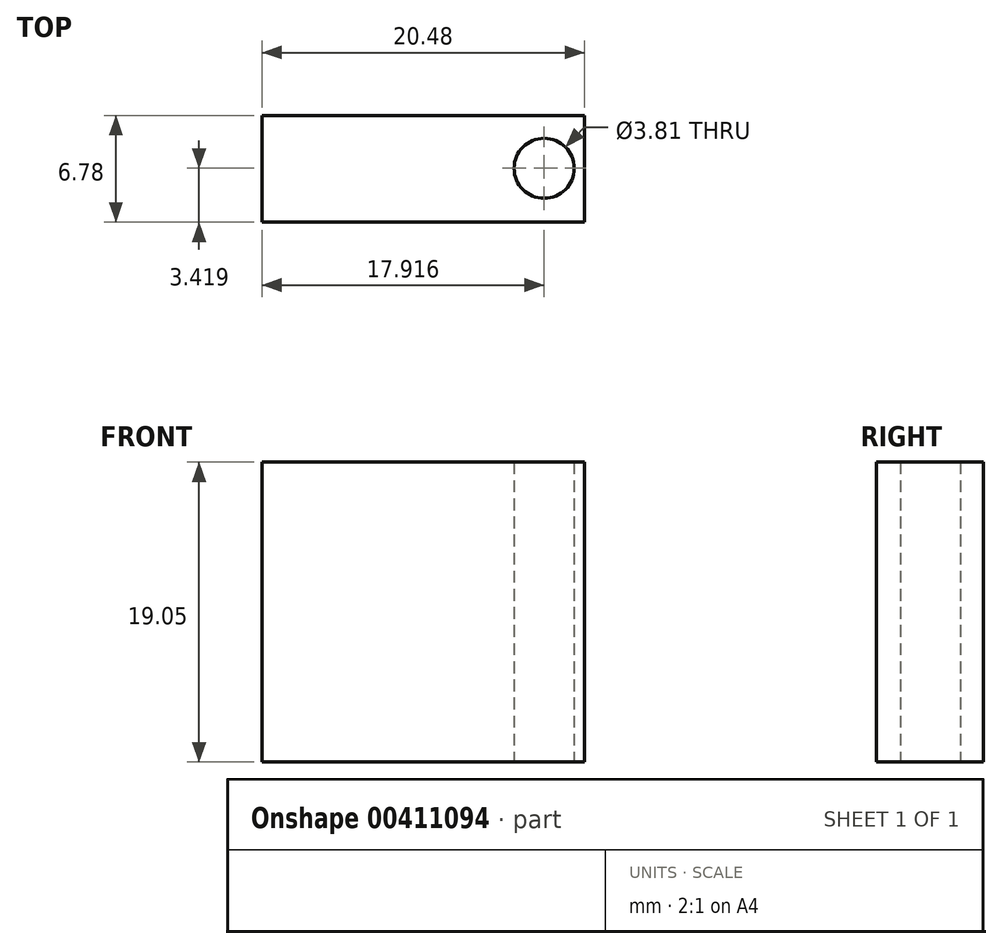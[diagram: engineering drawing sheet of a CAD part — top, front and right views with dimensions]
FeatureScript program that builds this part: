
annotation { "Feature Type Name" : "Feature", "Feature Type Description" : "" }
export const myFeature = defineFeature(function(context is Context, id is Id, definition is map)
    precondition{}
    {
        {
            var Q0;
            Q0=qCreatedBy(makeId("Top.planeOp"),FACE);
            var sketch = newSketch(context, id + "F0", { "sketchPlane" : qUnion([Q0])});
            skLineSegment(sketch, "E0.bottom", {"start": v(10.24, 3.39) * mm, "end": v(-10.24, 3.39) * mm});
            skLineSegment(sketch, "E0.top", {"start": v(10.24, -3.39) * mm, "end": v(-10.24, -3.39) * mm});
            skLineSegment(sketch, "E0.left", {"start": v(10.24, 3.39) * mm, "end": v(10.24, -3.39) * mm});
            skLineSegment(sketch, "E0.right", {"start": v(-10.24, 3.39) * mm, "end": v(-10.24, -3.39) * mm});
            skPoint(sketch, "E0.middle", {"position": v(0, 0) * mm});
            skCircle(sketch, "E1", {"center": v(-7.68, 0.03) * mm, "radius": 1.9 * mm});
            skCircle(sketch, "E2.MirrorC", {"center": v(7.68, 0.03) * mm, "radius": 1.9 * mm});
            skSolve(sketch);
        }
        {
            var Q0;
            Q0=makeQuery(id+"F0.imprint","IMPRINT",FACE,{"disambiguationData":[TD([[makeQuery(id+"F0.imprint","IMPRINT",EDGE,{"derivedFrom":sQuery(id+"F0.wireOp",EDGE,"E0.bottom")}),1.0]])]});
            extrude(context, id + "F1", {"entities" : qUnion([Q0]), "depth" : 3.8 * mm});
        }
        {
            var Q0;
            Q0=makeQuery(id+"F0.imprint","IMPRINT",FACE,{"disambiguationData":[TD([[makeQuery(id+"F0.imprint","IMPRINT",EDGE,{"derivedFrom":sQuery(id+"F0.wireOp",EDGE,"E1")}),1.0]])]});
            var Q1;
            Q1=makeQuery(id+"F0.imprint","IMPRINT",FACE,{"disambiguationData":[TD([[makeQuery(id+"F0.imprint","IMPRINT",EDGE,{"derivedFrom":sQuery(id+"F0.wireOp",EDGE,"E2.MirrorC")}),-1.0]])]});
            extrude(context, id + "F2", {"entities" : qUnion([Q0, Q1]), "operationType" : NewBodyOperationType.ADD, "depth" : 19.05 * mm});
        }
    });
